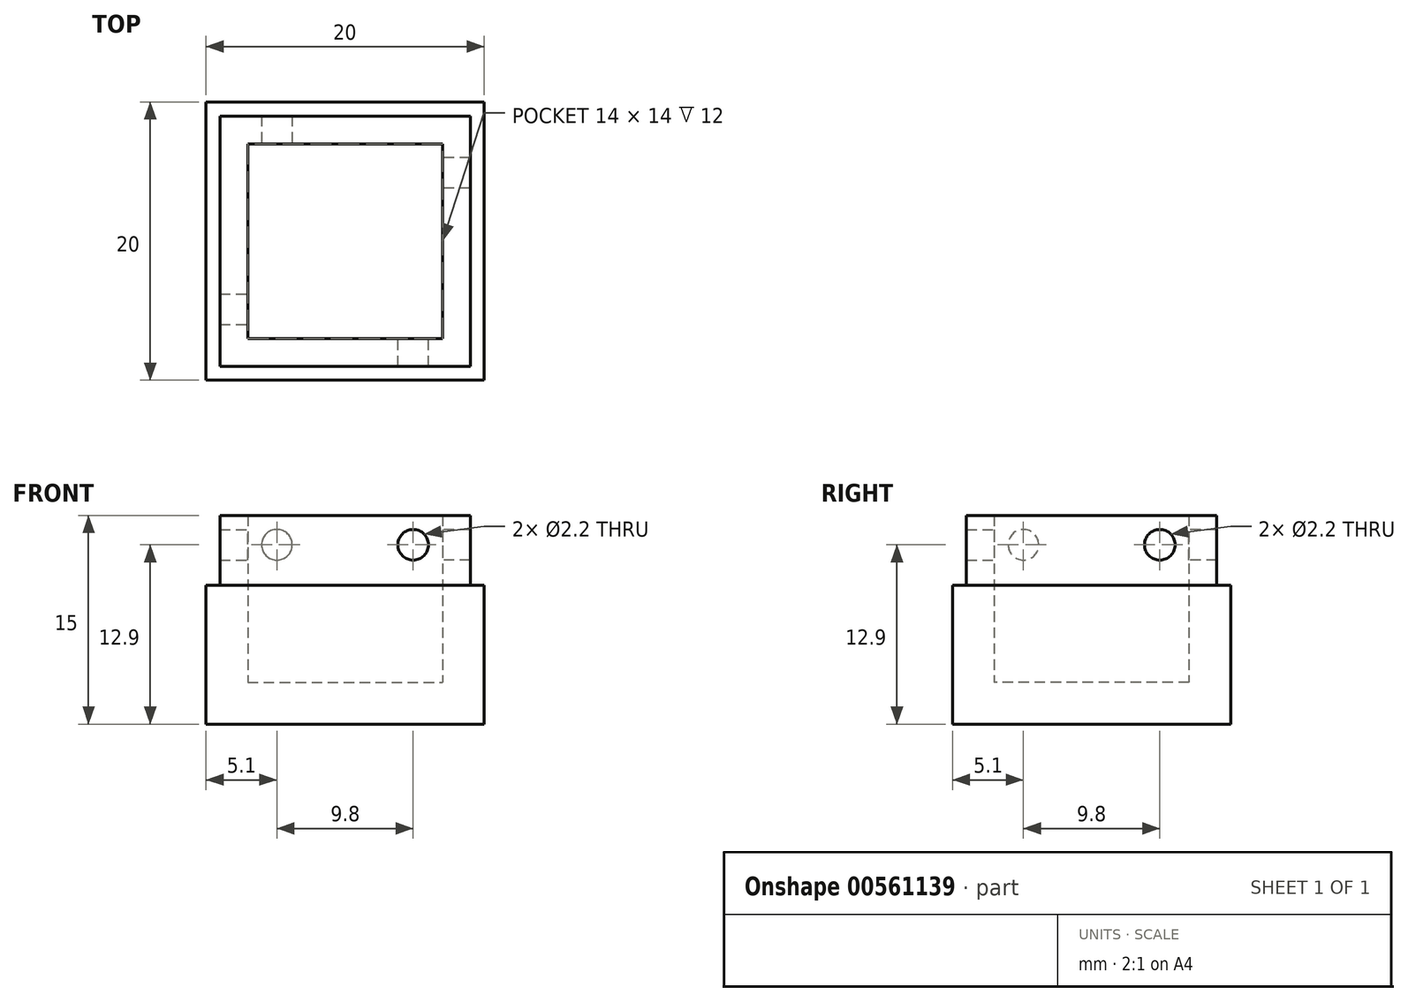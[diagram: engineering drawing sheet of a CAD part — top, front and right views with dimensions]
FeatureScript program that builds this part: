
annotation { "Feature Type Name" : "Feature", "Feature Type Description" : "" }
export const myFeature = defineFeature(function(context is Context, id is Id, definition is map)
    precondition{}
    {
        {
            assignVariable(context, id + "F0", {"name" : "height", "anyValue" : 7});
        }
        {
            assignVariable(context, id + "F1", {"name" : "wall_width", "anyValue" : 3});
        }
        {
            var Q0;
            Q0=qCreatedBy(makeId("Top.planeOp"),FACE);
            var sketch = newSketch(context, id + "F2", { "sketchPlane" : qUnion([Q0])});
            skLineSegment(sketch, "E0.bottom", {"start": v(0, 0) * mm, "end": v(20, 0) * mm});
            skLineSegment(sketch, "E0.top", {"start": v(0, -20) * mm, "end": v(20, -20) * mm});
            skLineSegment(sketch, "E0.left", {"start": v(0, 0) * mm, "end": v(0, -20) * mm});
            skLineSegment(sketch, "E0.right", {"start": v(20, 0) * mm, "end": v(20, -20) * mm});
            skSolve(sketch);
        }
        {
            var Q0;
            Q0=makeQuery(id+"F2.imprint","IMPRINT",FACE,{"disambiguationData":[TD([[makeQuery(id+"F2.imprint","IMPRINT",EDGE,{"derivedFrom":sQuery(id+"F2.wireOp",EDGE,"E0.bottom")}),-1.0]])]});
            extrude(context, id + "F3", {"entities" : qUnion([Q0]), "depth" : (getVariable(context, 'wall_width')) * mm, "offsetDistance" : 25 * mm});
        }
        {
            var Q0;
            Q0=makeQuery(id+"F3.opExtrude","CAP_FACE",FACE,{"disambiguationData":[OSD([sQuery(id+"F2.wireOp",EDGE,"E0.bottom"),sQuery(id+"F2.wireOp",EDGE,"E0.top"),sQuery(id+"F2.wireOp",EDGE,"E0.left"),sQuery(id+"F2.wireOp",EDGE,"E0.right")])],"isStart":false});
            var sketch = newSketch(context, id + "F4", { "sketchPlane" : qUnion([Q0])});
            skLineSegment(sketch, "E1.bottom", {"start": v(3, -3) * mm, "end": v(17, -3) * mm});
            skLineSegment(sketch, "E1.top", {"start": v(3, -17) * mm, "end": v(17, -17) * mm});
            skLineSegment(sketch, "E1.left", {"start": v(3, -3) * mm, "end": v(3, -17) * mm});
            skLineSegment(sketch, "E1.right", {"start": v(17, -3) * mm, "end": v(17, -17) * mm});
            skSolve(sketch);
        }
        {
            var Q0;
            Q0=makeQuery(id+"F4.imprint","IMPRINT",FACE,{"disambiguationData":[TD([[makeQuery(id+"F4.imprint","IMPRINT",EDGE,{"derivedFrom":sQuery(id+"F4.wireOp",EDGE,"E1.bottom")}),1.0]])]});
            extrude(context, id + "F5", {"entities" : qUnion([Q0]), "operationType" : NewBodyOperationType.ADD, "depth" : (getVariable(context, 'height')) * mm, "offsetDistance" : 25 * mm});
        }
        {
            assignVariable(context, id + "F6", {"name" : "lip_height", "anyValue" : 5});
        }
        {
            var Q0;
            Q0=makeQuery(id+"F5.opExtrude","CAP_FACE",FACE,{"disambiguationData":[OSD([sQuery(id+"F2.wireOp",EDGE,"E0.bottom"),sQuery(id+"F2.wireOp",EDGE,"E0.top"),sQuery(id+"F2.wireOp",EDGE,"E0.left"),sQuery(id+"F2.wireOp",EDGE,"E0.right"),sQuery(id+"F4.wireOp",EDGE,"E1.bottom"),sQuery(id+"F4.wireOp",EDGE,"E1.top"),sQuery(id+"F4.wireOp",EDGE,"E1.left"),sQuery(id+"F4.wireOp",EDGE,"E1.right")])],"isStart":false});
            var sketch = newSketch(context, id + "F7", { "sketchPlane" : qUnion([Q0])});
            skLineSegment(sketch, "E2.bottom", {"start": v(1, -1) * mm, "end": v(19, -1) * mm});
            skLineSegment(sketch, "E2.top", {"start": v(1, -19) * mm, "end": v(19, -19) * mm});
            skLineSegment(sketch, "E2.left", {"start": v(1, -1) * mm, "end": v(1, -19) * mm});
            skLineSegment(sketch, "E2.right", {"start": v(19, -1) * mm, "end": v(19, -19) * mm});
            skSolve(sketch);
        }
        {
            var Q0;
            Q0=makeQuery(id+"F7.imprint","IMPRINT",FACE,{"disambiguationData":[TD([[makeQuery(id+"F7.imprint","IMPRINT",EDGE,{"derivedFrom":sQuery(id+"F7.wireOp",EDGE,"E2.bottom")}),-1.0]])]});
            extrude(context, id + "F8", {"entities" : qUnion([Q0]), "operationType" : NewBodyOperationType.ADD, "depth" : (getVariable(context, 'lip_height')) * mm, "offsetDistance" : 25 * mm});
        }
        {
            var Q0;
            {var subQ0=sQuery(id+"F4.wireOp",EDGE,"E1.top");Q0=makeQuery(id+"F8.boolean.opBoolean","MERGE",FACE,{"derivedFrom":[makeQuery(id+"F5.opExtrude","SWEPT_FACE",FACE,{"disambiguationData":[OSD([subQ0])]}),makeQuery(id+"F8.opExtrude","SWEPT_FACE",FACE,{"disambiguationData":[OSD([subQ0])]})]});}
            var sketch = newSketch(context, id + "F9", { "sketchPlane" : qUnion([Q0])});
            skCircle(sketch, "E3", {"center": v(-14.9, 12.9) * mm, "radius": 1.1 * mm});
            skSolve(sketch);
        }
        {
            var Q0;
            Q0=makeQuery(id+"F9.imprint","IMPRINT",FACE,{"disambiguationData":[TD([[makeQuery(id+"F9.imprint","IMPRINT",EDGE,{"derivedFrom":sQuery(id+"F9.wireOp",EDGE,"E3")}),1.0]])]});
            extrude(context, id + "F10", {"entities" : qUnion([Q0]), "operationType" : NewBodyOperationType.REMOVE, "oppositeDirection" : true, "depth" : 2 * mm, "offsetDistance" : 25 * mm});
        }
        {
            var Q0;
            {var subQ0=sQuery(id+"F4.wireOp",EDGE,"E1.left");Q0=makeQuery(id+"F8.boolean.opBoolean","MERGE",FACE,{"derivedFrom":[makeQuery(id+"F5.opExtrude","SWEPT_FACE",FACE,{"disambiguationData":[OSD([subQ0])]}),makeQuery(id+"F8.opExtrude","SWEPT_FACE",FACE,{"disambiguationData":[OSD([subQ0])]})]});}
            var sketch = newSketch(context, id + "F11", { "sketchPlane" : qUnion([Q0])});
            skCircle(sketch, "E4", {"center": v(-14.9, 12.9) * mm, "radius": 1.1 * mm});
            skSolve(sketch);
        }
        {
            var Q0;
            Q0=makeQuery(id+"F11.imprint","IMPRINT",FACE,{"disambiguationData":[TD([[makeQuery(id+"F11.imprint","IMPRINT",EDGE,{"derivedFrom":sQuery(id+"F11.wireOp",EDGE,"E4")}),1.0]])]});
            extrude(context, id + "F12", {"entities" : qUnion([Q0]), "operationType" : NewBodyOperationType.REMOVE, "oppositeDirection" : true, "depth" : 3 * mm, "offsetDistance" : 25 * mm});
        }
        {
            var Q0;
            {var subQ0=sQuery(id+"F4.wireOp",EDGE,"E1.bottom");Q0=makeQuery(id+"F8.boolean.opBoolean","MERGE",FACE,{"derivedFrom":[makeQuery(id+"F5.opExtrude","SWEPT_FACE",FACE,{"disambiguationData":[OSD([subQ0])]}),makeQuery(id+"F8.opExtrude","SWEPT_FACE",FACE,{"disambiguationData":[OSD([subQ0])]})]});}
            var sketch = newSketch(context, id + "F13", { "sketchPlane" : qUnion([Q0])});
            skCircle(sketch, "E5", {"center": v(5.1, 12.9) * mm, "radius": 1.1 * mm});
            skSolve(sketch);
        }
        {
            var Q0;
            Q0=makeQuery(id+"F13.imprint","IMPRINT",FACE,{"disambiguationData":[TD([[makeQuery(id+"F13.imprint","IMPRINT",EDGE,{"derivedFrom":sQuery(id+"F13.wireOp",EDGE,"E5")}),1.0]])]});
            extrude(context, id + "F14", {"entities" : qUnion([Q0]), "operationType" : NewBodyOperationType.REMOVE, "oppositeDirection" : true, "depth" : 3 * mm, "offsetDistance" : 25 * mm});
        }
        {
            var Q0;
            {var subQ0=sQuery(id+"F4.wireOp",EDGE,"E1.right");Q0=makeQuery(id+"F8.boolean.opBoolean","MERGE",FACE,{"derivedFrom":[makeQuery(id+"F5.opExtrude","SWEPT_FACE",FACE,{"disambiguationData":[OSD([subQ0])]}),makeQuery(id+"F8.opExtrude","SWEPT_FACE",FACE,{"disambiguationData":[OSD([subQ0])]})]});}
            var sketch = newSketch(context, id + "F15", { "sketchPlane" : qUnion([Q0])});
            skCircle(sketch, "E6", {"center": v(5.1, 12.9) * mm, "radius": 1.1 * mm});
            skSolve(sketch);
        }
        {
            var Q0;
            Q0=makeQuery(id+"F15.imprint","IMPRINT",FACE,{"disambiguationData":[TD([[makeQuery(id+"F15.imprint","IMPRINT",EDGE,{"derivedFrom":sQuery(id+"F15.wireOp",EDGE,"E6")}),1.0]])]});
            extrude(context, id + "F16", {"entities" : qUnion([Q0]), "operationType" : NewBodyOperationType.REMOVE, "oppositeDirection" : true, "depth" : 3 * mm, "offsetDistance" : 25 * mm});
        }
    });
